# Revit family: Gira_021133
name_source: partatom
category: Electrical Fixtures
revit_build: Autodesk Revit 2017 (Build: 20160225_1515(x64)
units: mm (PartAtom-declared; Revit-internal decimal feet)

## family parameters
Cut with Voids When Loaded = No
Host = Face
Maintain Annotation Orientation = No
Part Type = Normal
Room Calculation Point = No
Round Connector Dimension = Use Diameter
Shared = No

## types (1)
- Gira_021133
    Anzahl der Einheiten = 1
    Anzahl der Einheiten horizontal = 1
    Anzahl der Einheiten vertikal = 1
    Available = Yes
    BIM (1) = https://media.live.bim.site
    Befestigungsart = Klemmbefestigung
    Category = Abdeckrahmen
    Data sheet (1) = https://katalog.gira.de
    Default Elevation = 1219 mm
    Description = Abdeckrahmen Gira E2 Edelstahl 1fach Hinweise : - Auch für Kanalinstallationen geeignet. - Abdeckrahmen (1- bis 5fach) in Verbindung mit Dichtungsset auch für die Montage wassergeschützt Unterputz IP44 geeignet.
    Farbe = edelstahl
    GTIN = 4010337019794
    Geeignet für Einbauinstallation = Nein
    Geeignet für Geräteeinbaukanal = Nein
    Geeignet für Unterflurkanaldose = Nein
    Geeignet für Unterputz-Installation = Ja
    HAN = 021133
    Halogenfrei = Nein
    HeinzeBIM = https://bimportal.heinze.de
    Kategorie = Abdeckrahmen
    Keynote = E2_Rahmen_1fach
    Manufacturer = Gira
    Manufacturer URL = https://www.gira.de
    Mit Klappdeckel = Nein
    Mit Montagerahmen = Nein
    Montagerichtung = horizontal und vertikal
    Name = Abdeckrahmen 1f Gira E2 Edelstahl
    Oberfläche = sonstige
    Region = DE
    Schutzart (IP) = IP20
    Textfeld/Beschriftungsfläche = Nein
    Transparent = Nein
    URL = http://katalog.gira.de
    Verfügbar = Ja
    Werkstoff = Metall
    Werkstoffgüte = edelstahl

## geometry (parser evidence)
native form markers: Blend x2, Sweep x3
no freeform markers — native parametric forms only
